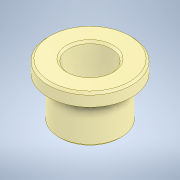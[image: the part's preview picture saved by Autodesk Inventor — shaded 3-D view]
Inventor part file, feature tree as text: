
AUTODESK INVENTOR PART (.ipt)
format: ipt  version: 2022 (Build 260153000, 153)  size: 134,144 bytes
history: native  units: mm
features: extrude x2, sketch x2, chamfer x1, projected_geometry x1
ambient origin geometry x8: Origin, YZ Plane, XZ Plane, XY Plane, X Axis, Y Axis, Z Axis, Center Point
bodies: Solid1 (feature_tree)
feature tree (6):
  extrude  "Extrusion1"  Depth=10.2mm
  extrude  "Extrusion2"  Depth=3.0mm
  chamfer  "Chamfer1"  Distance=3.0mm
  sketch  "Sketch1"  dims[d0=15.0mm d1=10.2mm]
  sketch  "Sketch2"  dims[d2=10.0mm d3=0.0mm d4=20.0mm d5=3.0mm d6=0.0mm d7=0.5mm d8=2.0mm d9=45.0deg]
  projected_geometry  "Projected Loop1"
